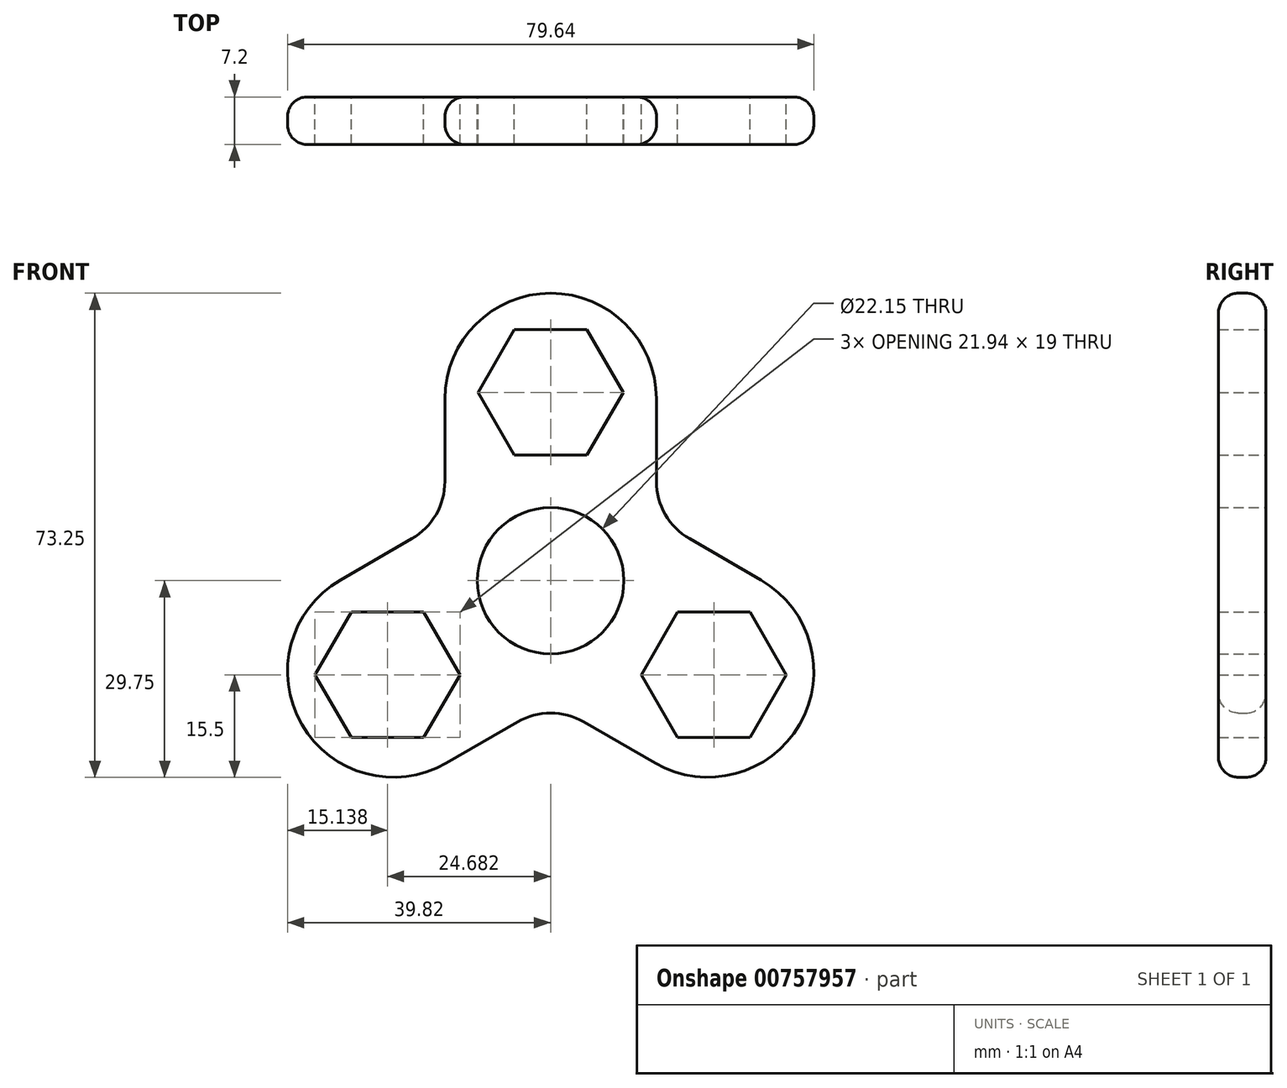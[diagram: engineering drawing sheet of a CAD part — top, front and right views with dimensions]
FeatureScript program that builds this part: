
annotation { "Feature Type Name" : "Feature", "Feature Type Description" : "" }
export const myFeature = defineFeature(function(context is Context, id is Id, definition is map)
    precondition{}
    {
        {
            var Q0;
            Q0=qCreatedBy(makeId("Front.planeOp"),FACE);
            var sketch = newSketch(context, id + "F0", { "sketchPlane" : qUnion([Q0])});
            skCircle(sketch, "E0", {"center": v(0, 0) * mm, "radius": 11.07 * mm});
            skArc(sketch, "E1", {"start": v(16, 27.5) * mm, "mid": v(0, 43.5) * mm, "end": v(-16, 27.5) * mm});
            skLineSegment(sketch, "E2", {"start": v(16, 27.5) * mm, "end": v(16, 15.01) * mm});
            skLineSegment(sketch, "E3.MirrorCS", {"start": v(-16, 27.5) * mm, "end": v(-16, 15.01) * mm});
            skPoint(sketch, "E4.visualSharp", {"position": v(0, -20.44) * mm});
            skLineSegment(sketch, "E5.1.0", {"start": v(-15.82, -27.6) * mm, "end": v(-5, -21.36) * mm});
            skArc(sketch, "E5.1.1", {"start": v(-31.82, 0.1) * mm, "mid": v(-37.67, -21.75) * mm, "end": v(-15.82, -27.6) * mm});
            skLineSegment(sketch, "E5.1.2", {"start": v(-31.82, 0.1) * mm, "end": v(-21, 6.35) * mm});
            skLineSegment(sketch, "E5.2.0", {"start": v(31.82, 0.1) * mm, "end": v(21, 6.35) * mm});
            skArc(sketch, "E5.2.1", {"start": v(15.82, -27.6) * mm, "mid": v(37.67, -21.75) * mm, "end": v(31.82, 0.1) * mm});
            skLineSegment(sketch, "E5.2.2", {"start": v(15.82, -27.6) * mm, "end": v(5, -21.36) * mm});
            skPoint(sketch, "E6.orphan", {"position": v(19.3, 7.33) * mm});
            skPoint(sketch, "E7.orphan", {"position": v(-19.3, 7.33) * mm});
            skPoint(sketch, "E8.orphan", {"position": v(-16, 13.05) * mm});
            skPoint(sketch, "E9.orphan", {"position": v(-3.3, -20.38) * mm});
            skPoint(sketch, "E10.orphan", {"position": v(3.3, -20.38) * mm});
            skPoint(sketch, "E11.orphan", {"position": v(16, 13.05) * mm});
            skPoint(sketch, "E12.visualSharp", {"position": v(-16, 9.24) * mm});
            skArc(sketch, "E12.filletArc", {"start": v(-21, 6.35) * mm, "mid": v(-17.34, 10.01) * mm, "end": v(-16, 15.01) * mm});
            skPoint(sketch, "E13.visualSharp", {"position": v(16, 9.24) * mm});
            skArc(sketch, "E13.filletArc", {"start": v(16, 15.01) * mm, "mid": v(17.34, 10.01) * mm, "end": v(21, 6.35) * mm});
            skPoint(sketch, "E14.visualSharp", {"position": v(0, -18.48) * mm});
            skArc(sketch, "E14.filletArc", {"start": v(5, -21.36) * mm, "mid": v(0, -20.02) * mm, "end": v(-5, -21.36) * mm});
            skCircle(sketch, "E15.cCircle", {"center": v(0, 28.5) * mm, "radius": 9.5 * mm, "construction": true});
            skLineSegment(sketch, "E15.0", {"start": v(-5.48, 38) * mm, "end": v(5.48, 38) * mm});
            skLineSegment(sketch, "E15.1", {"start": v(5.48, 38) * mm, "end": v(10.97, 28.5) * mm});
            skLineSegment(sketch, "E15.2", {"start": v(10.97, 28.5) * mm, "end": v(5.48, 19) * mm});
            skLineSegment(sketch, "E15.3", {"start": v(5.48, 19) * mm, "end": v(-5.48, 19) * mm});
            skLineSegment(sketch, "E15.4", {"start": v(-5.48, 19) * mm, "end": v(-10.97, 28.5) * mm});
            skLineSegment(sketch, "E15.5", {"start": v(-10.97, 28.5) * mm, "end": v(-5.48, 38) * mm});
            skPoint(sketch, "E15.0.midPoint", {"position": v(0, 38) * mm});
            skLineSegment(sketch, "E16.1.0", {"start": v(-30.17, -23.75) * mm, "end": v(-35.65, -14.25) * mm});
            skLineSegment(sketch, "E16.1.1", {"start": v(-19.2, -23.75) * mm, "end": v(-30.17, -23.75) * mm});
            skLineSegment(sketch, "E16.1.2", {"start": v(-13.71, -14.25) * mm, "end": v(-19.2, -23.75) * mm});
            skLineSegment(sketch, "E16.1.3", {"start": v(-19.2, -4.75) * mm, "end": v(-13.71, -14.25) * mm});
            skLineSegment(sketch, "E16.1.4", {"start": v(-30.17, -4.75) * mm, "end": v(-19.2, -4.75) * mm});
            skLineSegment(sketch, "E16.1.5", {"start": v(-35.65, -14.25) * mm, "end": v(-30.17, -4.75) * mm});
            skLineSegment(sketch, "E16.2.0", {"start": v(35.65, -14.25) * mm, "end": v(30.17, -23.75) * mm});
            skLineSegment(sketch, "E16.2.1", {"start": v(30.17, -4.75) * mm, "end": v(35.65, -14.25) * mm});
            skLineSegment(sketch, "E16.2.2", {"start": v(19.2, -4.75) * mm, "end": v(30.17, -4.75) * mm});
            skLineSegment(sketch, "E16.2.3", {"start": v(13.71, -14.25) * mm, "end": v(19.2, -4.75) * mm});
            skLineSegment(sketch, "E16.2.4", {"start": v(19.2, -23.75) * mm, "end": v(13.71, -14.25) * mm});
            skLineSegment(sketch, "E16.2.5", {"start": v(30.17, -23.75) * mm, "end": v(19.2, -23.75) * mm});
            skSolve(sketch);
        }
        {
            var Q0;
            Q0 = qSketchRegion(id + "F0", true);
            extrude(context, id + "F1", {"entities" : qUnion([Q0]), "depth" : 7.2 * mm, "offsetDistance" : 25 * mm});
        }
        {
            var Q0;
            Q0=makeQuery(id+"F1.opExtrude","CAP_EDGE",EDGE,{"disambiguationData":[OSD([sQuery(id+"F0.wireOp",EDGE,"E3.MirrorCS")])],"isStart":false});
            var Q1;
            Q1=makeQuery(id+"F1.opExtrude","CAP_EDGE",EDGE,{"disambiguationData":[OSD([sQuery(id+"F0.wireOp",EDGE,"E1")])],"isStart":true});
            fillet(context, id + "F2", {"entities" : qUnion([Q0, Q1]), "radius" : 3 * mm, "tangentPropagation" : true, "allowEdgeOverflow" : false});
        }
    });
